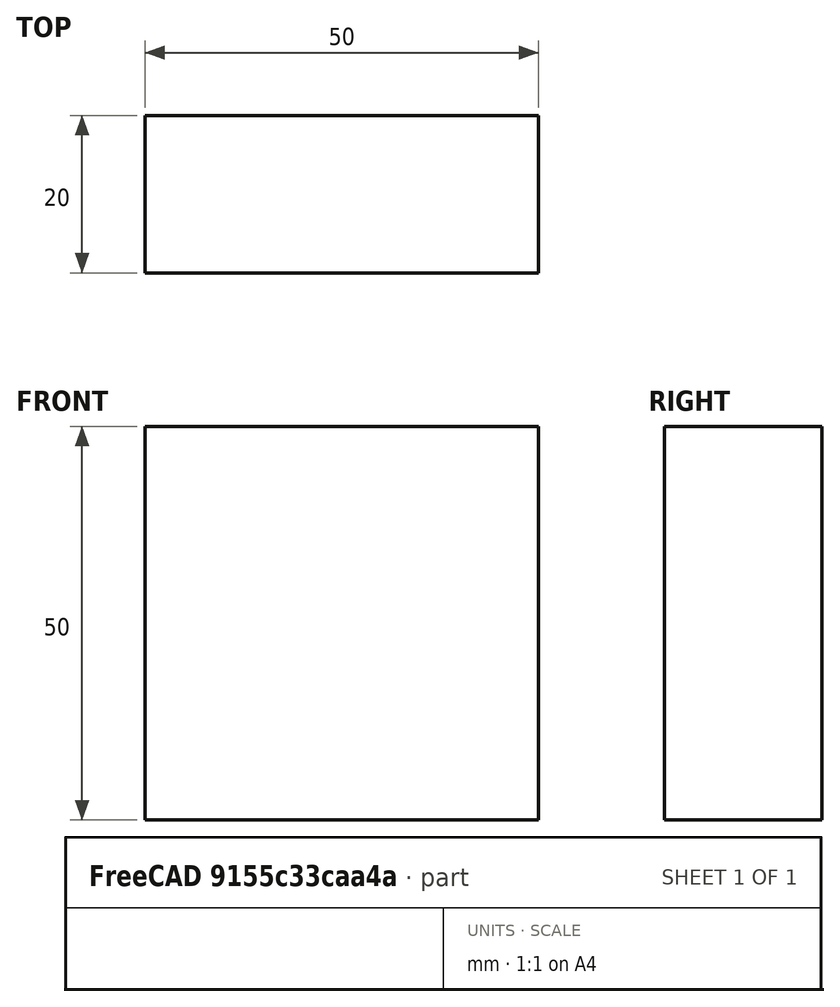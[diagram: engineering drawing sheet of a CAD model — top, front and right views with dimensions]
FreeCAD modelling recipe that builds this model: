
FCSTD DOCUMENT  (FreeCAD 0.15R4671 (Git))
Label: Flat Bar 50x20 EN10058 S235JR
License: All rights reserved
LicenseURL: http://en.wikipedia.org/wiki/All_rights_reserved
objects: Sketcher::SketchObject×1, Part::Extrusion×1
note: 2 computed .brp shape members not serialized (recipe doc carries the construction recipe); baked Part::Feature solids carry a one-line shape summary decoded from their .brp

FEATURE [Sketcher::SketchObject] Sketch
  sketch-geometry (4):
    g0: LineSegment StartX=-25 StartY=-10 StartZ=0 EndX=25 EndY=-10 EndZ=0
    g1: LineSegment StartX=25 StartY=-10 StartZ=0 EndX=25 EndY=10 EndZ=0
    g2: LineSegment StartX=25 StartY=10 StartZ=0 EndX=-25 EndY=10 EndZ=0
    g3: LineSegment StartX=-25 StartY=10 StartZ=0 EndX=-25 EndY=-10 EndZ=0
  constraints (12):
    c: Coincident(g0,g1)
    c: Coincident(g1,g2)
    c: Coincident(g2,g3)
    c: Coincident(g3,g0)
    c: Horizontal(g0)
    c: Horizontal(g2)
    c: Vertical(g1)
    c: Vertical(g3)
    c: Symmetric(g1,g2,g-2)
    c: Symmetric(g0,g1,g-1)
    c: DistanceY(g1) = 20
    c: DistanceX(g0) = 50
FEATURE [Part::Extrusion] Extrude  label="Flat Bar 50x20 EN10058 S235JR"
  Base = -> Sketch
  Dir = (0,0,50)
  Solid = true
